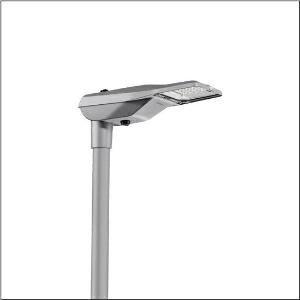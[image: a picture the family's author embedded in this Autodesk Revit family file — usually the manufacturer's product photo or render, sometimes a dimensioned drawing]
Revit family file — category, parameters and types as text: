
# Revit family: streetlight_sl_21_iq_micro___stw1_0a_5xe1e31y08cb_f1b3
name_source: partatom
category: Lighting Fixtures
units: mm (PartAtom-declared; Revit-internal decimal feet)

## family parameters
Cut with Voids When Loaded = No
Host = Face
Light Source = No
Part Type = Normal
Room Calculation Point = No
Round Connector Dimension = Use Diameter
Shared = No

## types (1)
- --- (1 x LED, 2880 lm, 19.1 W, 3000K)
    Apparent Load = 19 VA
    CIE Flux Codes = 38 75 98 100 100
    Color Rendering = 70
    Color Temperature = 3000K
    Default Elevation = 1800 mm
    Description = Streetlight SL 21 iQ micro, mast luminaire, primary light control with lens, of PMMA, primary optical cover: cover, of toughened safety glass, transparent, light distribution: STW1.0a, light emission: direct distribution, primary light characteristic: asymmetric, installation type: post-top, side-entry, LED, High Power LED, rated luminous flux: 2.880lm, luminous efficacy: 151lm/W, light colour: 730, colour temperature: 3000K, control: pre-setting: logarithmic dimming characteristic, Street-Remote, Auto-Match, Temp-Guard, Lumen-Switch, Night-Set, Smart-Wire, Light-Fading, Desk-Remote (wireless, voltage-free reading and setting of iQ features in the workshop via application-optimized NFC function/RFID function), optimised constant luminous flux control (CLO 2.0), mains connection: 220..240V, AC, 50/60Hz, start of lifetime: 19W, end of service life: 20W, reduction: 9W, luminaire housing, of diecast aluminium, powder-coated, Siteco® metallic grey (DB 702S), corrosivity category C5 mid according to DIN EN ISO 12944, please order mast flange separately, inclination adjustable: 0°, 5°, 10°, 15°, sealing non-destructively replaceable, multi-level sealing system, length: 528mm, width: 235mm, height: 110mm, mast flange for spigot size: 42mm (side-entry): 5XC10008XM4, 60/48mm (side-entry/post-top): 5XC10108XM2, 76/60mm (side-entry/post-top): 5XC10108XM1, Smart Interface below and above, protection rating (complete): IP66, insulation class (complete): insulation class II (safety insulation), certification: CE, ENEC, ENEC+, VDE, impact resistance: IK09, permissible operating ambient temperature for outdoor applications: -40..+50°C, standard-compliant lighting for roads and squares, packaging unit: 1 piece

Light Distribution: STW1.0a
    Height = 110 mm
    Lamp = 1 x LED
    Lamp Light Flux = 2880 lm
    Lamp Power = 19.1 W
    Lamp count = 1
    Length = 528 mm
    Luminous efficacy = 151 lm/W
    Manufacturer = Siteco
    ModVariant = No
    Model = 5XE1E31Y08CB
    Number of Poles = 1
    OnlyDefault = Yes
    Power Factor = 1
    Product Name = Streetlight SL 21 iQ micro | STW1.0a
    Product group = mast luminaire | pylon top
    ProductGroupID = 6100
    Protection Class = Protection class II
    Protection Degree = IP 66
    RLX_Detail_Level = 1
    RLX_Emergency_Light_Flux = 0 lm
    RLX_Emergency_Type = 0
    RLX_Emergency_Type_DB = No
    RlxData = <blob elided: 99473 chars, md5=808a2c3a>
    Socket = socket
    Standby Power = 0 W
    System Light Flux = 2880 lm
    System Power = 19 W
    Type Comments = factory setting: luminous flux: 100 % | dim-lin: 254 | 387 mA
    Type Image = l_1007239.jpg
    URL = http://relux.com
    VarID = @adj_083263
    Voltage = 0 V
    Weight = 0.00 kg
    Width = 235 mm

## geometry (parser evidence)
native form markers: Blend x4, Sweep x10
no freeform markers — native parametric forms only
